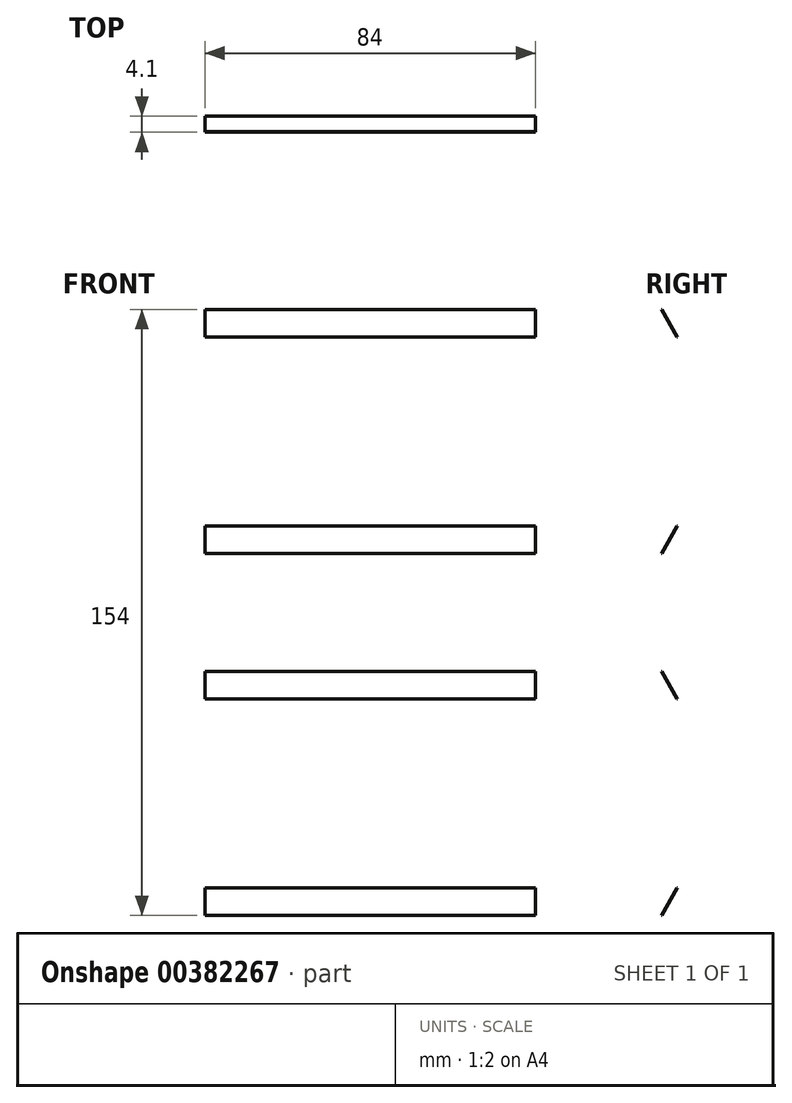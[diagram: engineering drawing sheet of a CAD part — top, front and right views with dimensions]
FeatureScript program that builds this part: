
annotation { "Feature Type Name" : "Feature", "Feature Type Description" : "" }
export const myFeature = defineFeature(function(context is Context, id is Id, definition is map)
    precondition{}
    {
        {
            var Q0;
            Q0=qCreatedBy(makeId("Right.planeOp"),FACE);
            var sketch = newSketch(context, id + "F0", { "sketchPlane" : qUnion([Q0])});
            skPoint(sketch, "E0", {"position": v(0, 0) * mm});
            skPoint(sketch, "E1", {"position": v(0, -22) * mm});
            skPoint(sketch, "E2", {"position": v(0, -70) * mm});
            skPoint(sketch, "E3", {"position": v(0, -15) * mm});
            skPoint(sketch, "E4", {"position": v(0, -77) * mm});
            skPoint(sketch, "E5", {"position": v(-4, -15) * mm});
            skPoint(sketch, "E6", {"position": v(-4, -77) * mm});
            skLineSegment(sketch, "E7", {"start": v(-4, -15) * mm, "end": v(0, -22) * mm});
            skPoint(sketch, "E8", {"position": v(-0.1, -22) * mm});
            skPoint(sketch, "E9", {"position": v(-4.1, -15) * mm});
            skLineSegment(sketch, "E10", {"start": v(-4.1, -15) * mm, "end": v(-0.1, -22) * mm});
            skLineSegment(sketch, "E11", {"start": v(-0.1, -22) * mm, "end": v(0, -22) * mm});
            skLineSegment(sketch, "E12", {"start": v(-4.1, -15) * mm, "end": v(-4, -15) * mm});
            skPoint(sketch, "E13", {"position": v(0, -46) * mm});
            skPoint(sketch, "E14", {"position": v(-23.23, -46) * mm});
            skLineSegment(sketch, "E15", {"start": v(-23.23, -46) * mm, "end": v(31.18, -46) * mm});
            skLineSegment(sketch, "E16.MirrorCS", {"start": v(-23.23, -46) * mm, "end": v(39.36, -39.3) * mm});
            skLineSegment(sketch, "E17.MirrorCS", {"start": v(-4, -77) * mm, "end": v(0, -70) * mm});
            skLineSegment(sketch, "E18.MirrorCS", {"start": v(-4.1, -77) * mm, "end": v(-0.1, -70) * mm});
            skLineSegment(sketch, "E19", {"start": v(-4.1, -77) * mm, "end": v(-4, -77) * mm});
            skLineSegment(sketch, "E20", {"start": v(-0.1, -70) * mm, "end": v(0, -70) * mm});
            skLineSegment(sketch, "E21", {"start": v(-70.49, 0) * mm, "end": v(84.5, 0) * mm});
            skLineSegment(sketch, "E22.MirrorCS", {"start": v(-4, 15) * mm, "end": v(0, 22) * mm});
            skLineSegment(sketch, "E23.MirrorCS", {"start": v(-4.1, 15) * mm, "end": v(-0.1, 22) * mm});
            skLineSegment(sketch, "E24.MirrorCS", {"start": v(-0.1, 22) * mm, "end": v(0, 22) * mm});
            skLineSegment(sketch, "E25.MirrorCS", {"start": v(-4, 77) * mm, "end": v(0, 70) * mm});
            skLineSegment(sketch, "E26.MirrorCS", {"start": v(-4.1, 77) * mm, "end": v(-0.1, 70) * mm});
            skLineSegment(sketch, "E27.MirrorCS", {"start": v(-0.1, 70) * mm, "end": v(0, 70) * mm});
            skLineSegment(sketch, "E28.MirrorCS", {"start": v(-4.1, 77) * mm, "end": v(-4, 77) * mm});
            skLineSegment(sketch, "E29", {"start": v(-4.1, 15) * mm, "end": v(-4, 15) * mm});
            skLineSegment(sketch, "E30", {"start": v(0, 77) * mm, "end": v(0, -77) * mm});
            skLineSegment(sketch, "E31.MirrorCS", {"start": v(0.1, -70) * mm, "end": v(0, -70) * mm});
            skLineSegment(sketch, "E32.MirrorCS", {"start": v(4.1, -77) * mm, "end": v(0.1, -70) * mm});
            skLineSegment(sketch, "E33.MirrorCS", {"start": v(4, -77) * mm, "end": v(0, -70) * mm});
            skLineSegment(sketch, "E34.MirrorCS", {"start": v(4.1, -77) * mm, "end": v(4, -77) * mm});
            skLineSegment(sketch, "E35.MirrorCS", {"start": v(4.1, -15) * mm, "end": v(0.1, -22) * mm});
            skLineSegment(sketch, "E36.MirrorCS", {"start": v(4, -15) * mm, "end": v(0, -22) * mm});
            skLineSegment(sketch, "E37.MirrorCS", {"start": v(0.1, -22) * mm, "end": v(0, -22) * mm});
            skLineSegment(sketch, "E38.MirrorCS", {"start": v(4.1, -15) * mm, "end": v(4, -15) * mm});
            skLineSegment(sketch, "E39.MirrorCS", {"start": v(4.1, 15) * mm, "end": v(4, 15) * mm});
            skLineSegment(sketch, "E40.MirrorCS", {"start": v(4.1, 15) * mm, "end": v(0.1, 22) * mm});
            skLineSegment(sketch, "E41.MirrorCS", {"start": v(4, 15) * mm, "end": v(0, 22) * mm});
            skLineSegment(sketch, "E42.MirrorCS", {"start": v(0.1, 22) * mm, "end": v(0, 22) * mm});
            skLineSegment(sketch, "E43.MirrorCS", {"start": v(0.1, 70) * mm, "end": v(0, 70) * mm});
            skLineSegment(sketch, "E44.MirrorCS", {"start": v(4.1, 77) * mm, "end": v(0.1, 70) * mm});
            skLineSegment(sketch, "E45.MirrorCS", {"start": v(4, 77) * mm, "end": v(0, 70) * mm});
            skLineSegment(sketch, "E46.MirrorCS", {"start": v(4.1, 77) * mm, "end": v(4, 77) * mm});
            skSolve(sketch);
        }
        {
            var Q0;
            Q0=makeQuery(id+"F0.imprint","IMPRINT",FACE,{"disambiguationData":[TD([[makeQuery(id+"F0.imprint","IMPRINT",EDGE,{"derivedFrom":sQuery(id+"F0.wireOp",EDGE,"E7")}),-1.0]])]});
            var Q1;
            Q1=makeQuery(id+"F0.imprint","IMPRINT",FACE,{"disambiguationData":[TD([[makeQuery(id+"F0.imprint","IMPRINT",EDGE,{"derivedFrom":sQuery(id+"F0.wireOp",EDGE,"E22.MirrorCS")}),1.0]])]});
            var Q2;
            Q2=makeQuery(id+"F0.imprint","IMPRINT",FACE,{"disambiguationData":[TD([[makeQuery(id+"F0.imprint","IMPRINT",EDGE,{"derivedFrom":sQuery(id+"F0.wireOp",EDGE,"E25.MirrorCS")}),-1.0]])]});
            var Q3;
            Q3=makeQuery(id+"F0.imprint","IMPRINT",FACE,{"disambiguationData":[TD([[makeQuery(id+"F0.imprint","IMPRINT",EDGE,{"derivedFrom":sQuery(id+"F0.wireOp",EDGE,"E17.MirrorCS")}),1.0]])]});
            extrude(context, id + "F1", {"entities" : qUnion([Q0, Q1, Q2, Q3]), "depth" : 84 * mm, "symmetric" : true});
        }
    });
